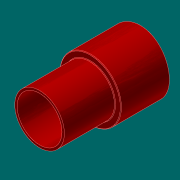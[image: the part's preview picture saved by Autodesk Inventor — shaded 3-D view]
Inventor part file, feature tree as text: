
AUTODESK INVENTOR PART (.ipt)
format: ipt  version: 2017.3 (Build 213257000, 257)  size: 119,296 bytes
history: native  units: in
note: dims shown in document units (in); Inventor stores cm internally (conversion verified against a paired STEP export)
features: extrude x3, sketch x2, fillet x1, chamfer x1
ambient origin geometry x8: Origin, YZ Plane, XZ Plane, XY Plane, X Axis, Y Axis, Z Axis, Center Point
bodies: Solid1 (feature_tree)
feature tree (7):
  sketch  "Sketch1"  dims[d0=2.88in d1=2.5984in]
  extrude  "Extrusion1"  Depth=2.5984in
  extrude  "Extrusion4"  Depth=0.0312in
  extrude  "Extrusion3"  Depth=0.0312in TaperAngle=0.0deg
  fillet  "Fillet2"  Radius=3.5625in
  chamfer  "Chamfer2"  Distance=18.3125in
  sketch  "Sketch3"  dims[d2=21.25in d3=0.0in d7=31.0in d8=0.5in d9=0.0in d11=3.5625in d12=18.3125in d13=0.0in d17=0.0312in d18=0.0312in d19=0.125in d20=45.0deg]
